# Revit family: Tairmo Ganzglas EA-L
name_source: partatom
category: Windows
revit_build: Autodesk Revit 2014 (Build: 20130308_1515(x64)
units: mm (PartAtom-declared; Revit-internal decimal feet)

## types (1)
- Tairmo Ganzglas EA-L
    Actual_Blade_height = 292 mm
    Actual_height = 3000 mm  [stored 9.84252 ft]
    Actual_width = 1500 mm
    Actuator(Electric, Manual, Pneumatic) = EA-L
    Actuator_horizontal_position = 1470 mm
    Angle_ = 75.00°
    Angle_opening = 75.00°
    Array_distance = 292 mm
    Array_visible = Yes
    B1 = 60 mm  [stored 0.19685 ft]
    B2 = 60 mm  [stored 0.19685 ft]
    Blade_height = 292 mm
    Blade_origin = 158 mm
    Blade_width = 1380 mm
    Default Sill Height = 800 mm  [stored 2.62467 ft]
    Depth = 66 mm  [stored 0.216535 ft]
    Frame_material = Aluminum, Anodized Silver
    Glass_material = Glass
    H1 = 28 mm  [stored 0.0918635 ft]
    H2 = 28 mm  [stored 0.0918635 ft]
    Height = 3000 mm  [stored 9.84252 ft]
    Main_visible = No
    No. of Blades = 10
    Numbers = 10
    PRACTICAL NUMBER OF BLADES = OKAY
    TrimProjection = 50 mm  [stored 0.164042 ft]
    Wall Closure = By host
    Width = 1500 mm

note: [stored X ft] marks values corroborated as IEEE doubles in the binary element streams (Revit-internal decimal feet)

## geometry (parser evidence)
native form markers: Sweep x25
no freeform markers — native parametric forms only
